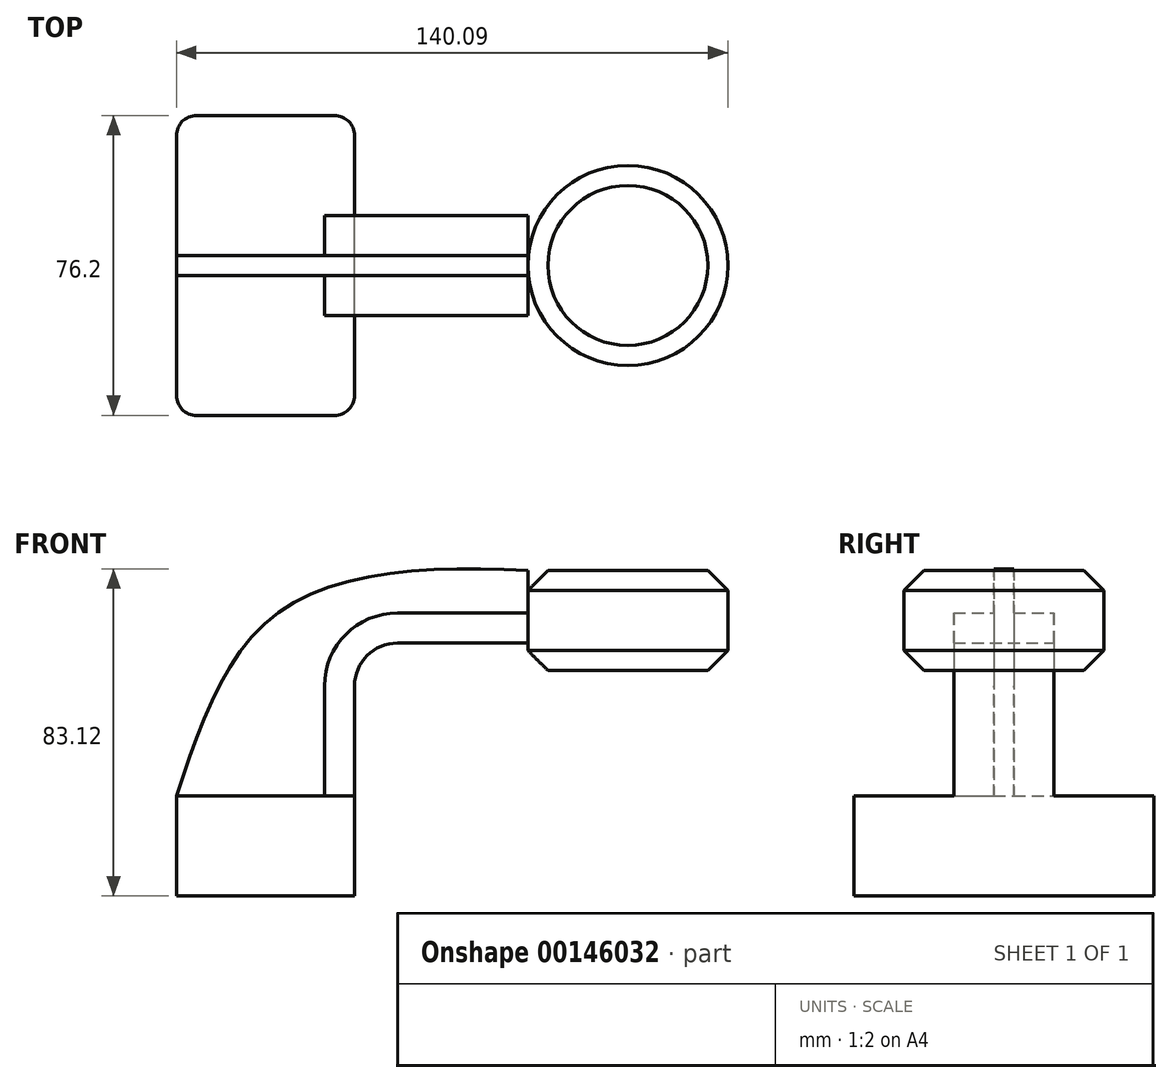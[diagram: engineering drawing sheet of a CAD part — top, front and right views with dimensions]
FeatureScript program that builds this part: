
annotation { "Feature Type Name" : "Feature", "Feature Type Description" : "" }
export const myFeature = defineFeature(function(context is Context, id is Id, definition is map)
    precondition{}
    {
        {
            var Q0;
            Q0=qCreatedBy(makeId("Front.planeOp"),FACE);
            var sketch = newSketch(context, id + "F0", { "sketchPlane" : qUnion([Q0])});
            skLineSegment(sketch, "E0.bottom", {"start": v(-44.29, 0) * mm, "end": v(0.94, 0) * mm});
            skLineSegment(sketch, "E0.top", {"start": v(-44.29, 25.4) * mm, "end": v(0.94, 25.4) * mm});
            skLineSegment(sketch, "E0.left", {"start": v(-44.29, 0) * mm, "end": v(-44.29, 25.4) * mm});
            skLineSegment(sketch, "E0.right", {"start": v(0.94, 0) * mm, "end": v(0.94, 25.4) * mm});
            skLineSegment(sketch, "E1.bottom", {"start": v(45, 57.3) * mm, "end": v(95.8, 57.3) * mm});
            skLineSegment(sketch, "E1.top", {"start": v(45, 82.7) * mm, "end": v(95.8, 82.7) * mm});
            skLineSegment(sketch, "E1.left", {"start": v(45, 57.3) * mm, "end": v(45, 82.7) * mm});
            skLineSegment(sketch, "E1.right", {"start": v(95.8, 57.3) * mm, "end": v(95.8, 82.7) * mm});
            skLineSegment(sketch, "E2", {"start": v(-6.68, 25.4) * mm, "end": v(-6.68, 53.34) * mm});
            skLineSegment(sketch, "E3", {"start": v(56.13, 71.92) * mm, "end": v(11.9, 71.92) * mm});
            skArc(sketch, "E4", {"start": v(11.9, 71.92) * mm, "mid": v(-1.24, 66.48) * mm, "end": v(-6.68, 53.34) * mm});
            skLineSegment(sketch, "E5.0", {"start": v(0.94, 25.4) * mm, "end": v(0.94, 53.34) * mm});
            skArc(sketch, "E5.1", {"start": v(11.9, 64.3) * mm, "mid": v(4.15, 61.08) * mm, "end": v(0.94, 53.34) * mm});
            skLineSegment(sketch, "E5.2", {"start": v(56.13, 64.3) * mm, "end": v(11.9, 64.3) * mm});
            skPoint(sketch, "E6.1.internal.snap0", {"position": v(34.01, 71.92) * mm});
            skFitSpline(sketch, "E6", {"points": [v(45, 82.7) * mm, v(-18.56, 71.92) * mm, v(-44.29, 25.4) * mm], "startDerivative": vector(-138.47, 7.17) * mm, "endDerivative": vector(-38.43, -114.84) * mm});
            skLineSegment(sketch, "E7", {"start": v(70.4, 57.3) * mm, "end": v(70.4, 82.7) * mm});
            skLineSegment(sketch, "E8", {"start": v(56.13, 71.92) * mm, "end": v(56.13, 64.3) * mm});
            skSolve(sketch);
        }
        {
            var Q0;
            Q0=makeQuery(id+"F0.imprint","IMPRINT",FACE,{"disambiguationData":[TD([[makeQuery(id+"F0.imprint","IMPRINT",EDGE,{"derivedFrom":sQuery(id+"F0.wireOp",EDGE,"E0.bottom")}),1.0]])]});
            extrude(context, id + "F1", {"entities" : qUnion([Q0]), "endBound" : BoundingType.SYMMETRIC, "depth" : 76.2 * mm});
        }
        {
            var Q0;
            {var subQ1=sQuery(id+"F0.wireOp",EDGE,"E2");Q0=makeQuery(id+"F0.imprint","IMPRINT",FACE,{"disambiguationData":[TD([[makeQuery(id+"F0.imprint","IMPRINT",EDGE,{"derivedFrom":subQ1}),1.0]])]});}
            extrude(context, id + "F2", {"entities" : qUnion([Q0]), "operationType" : NewBodyOperationType.ADD, "endBound" : BoundingType.SYMMETRIC, "depth" : 5.08 * mm});
        }
        {
            var Q0;
            {var subQ0=sQuery(id+"F0.wireOp",EDGE,"E1.right");Q0=makeQuery(id+"F0.imprint","IMPRINT",FACE,{"disambiguationData":[TD([[makeQuery(id+"F0.imprint","IMPRINT",EDGE,{"derivedFrom":subQ0}),1.0]])]});}
            var Q1;
            Q1=sQuery(id+"F0.wireOp",EDGE,"E7");
            revolve(context, id + "F3", {"operationType" : NewBodyOperationType.ADD, "entities" : qUnion([Q0]), "axis" : qUnion([Q1]), "revolveType" : RevolveType.FULL});
        }
        {
            var Q0;
            {var subQ2=sQuery(id+"F0.wireOp",EDGE,"E2");Q0=makeQuery(id+"F0.imprint","IMPRINT",FACE,{"disambiguationData":[TD([[makeQuery(id+"F0.imprint","IMPRINT",EDGE,{"derivedFrom":subQ2}),-1.0]])]});}
            extrude(context, id + "F4", {"entities" : qUnion([Q0]), "operationType" : NewBodyOperationType.ADD, "endBound" : BoundingType.SYMMETRIC, "depth" : 25.4 * mm});
        }
        {
            var Q0;
            Q0=makeQuery(id+"F1.opExtrude","CAP_EDGE",EDGE,{"disambiguationData":[OSD([sQuery(id+"F0.wireOp",EDGE,"E0.left")])],"isStart":false});
            var Q1;
            Q1=makeQuery(id+"F1.opExtrude","CAP_EDGE",EDGE,{"disambiguationData":[OSD([sQuery(id+"F0.wireOp",EDGE,"E0.right")])],"isStart":false});
            var Q2;
            Q2=makeQuery(id+"F1.opExtrude","CAP_EDGE",EDGE,{"disambiguationData":[OSD([sQuery(id+"F0.wireOp",EDGE,"E0.right")])],"isStart":true});
            var Q3;
            Q3=makeQuery(id+"F1.opExtrude","CAP_EDGE",EDGE,{"disambiguationData":[OSD([sQuery(id+"F0.wireOp",EDGE,"E0.left")])],"isStart":true});
            fillet(context, id + "F5", {"entities" : qUnion([Q0, Q1, Q2, Q3]), "radius" : 5.08 * mm, "tangentPropagation" : true, "allowEdgeOverflow" : false});
        }
        {
            var Q0;
            Q0=makeQuery(id+"F3.opRevolve","SWEPT_FACE",FACE,{"disambiguationData":[OSD([sQuery(id+"F0.wireOp",EDGE,"E1.top")])]});
            var Q1;
            Q1=makeQuery(id+"F3.opRevolve","SWEPT_FACE",FACE,{"disambiguationData":[OSD([sQuery(id+"F0.wireOp",EDGE,"E1.bottom")])]});
            chamfer(context, id + "F6", {"entities" : qUnion([Q0, Q1]), "width" : 5.08 * mm, "tangentPropagation" : true});
        }
    });
